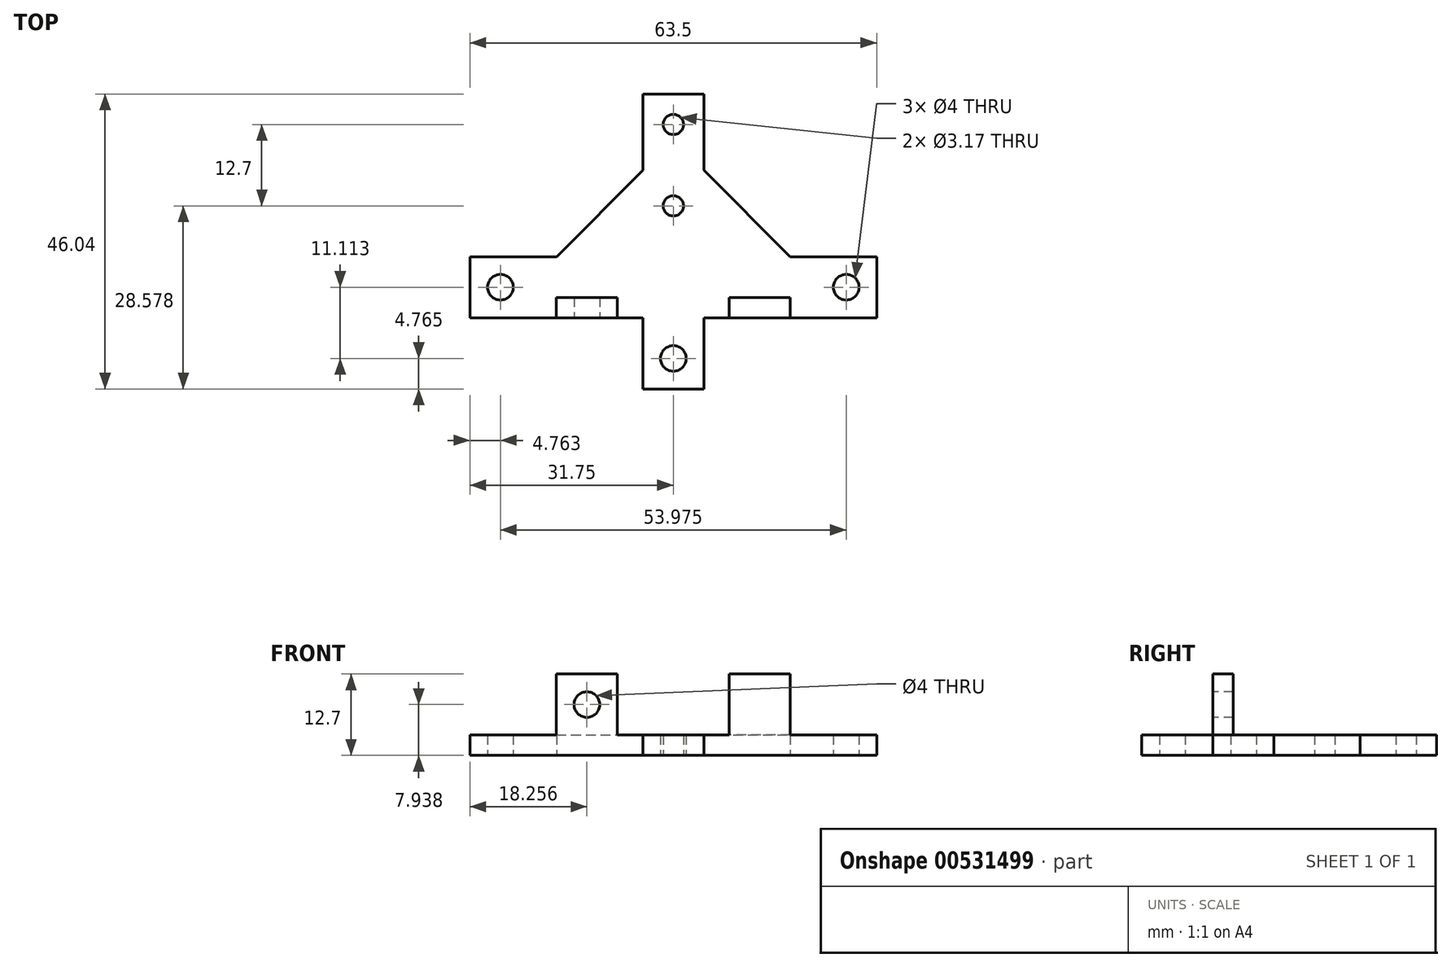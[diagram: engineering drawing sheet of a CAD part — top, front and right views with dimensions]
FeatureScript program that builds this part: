
annotation { "Feature Type Name" : "Feature", "Feature Type Description" : "" }
export const myFeature = defineFeature(function(context is Context, id is Id, definition is map)
    precondition{}
    {
        {
            var Q0;
            Q0=qCreatedBy(makeId("Top.planeOp"),FACE);
            var sketch = newSketch(context, id + "F0", { "sketchPlane" : qUnion([Q0])});
            skLineSegment(sketch, "E0.bottom", {"start": v(0, 0) * mm, "end": v(13.52, 0) * mm});
            skLineSegment(sketch, "E0.top", {"start": v(0, -9.53) * mm, "end": v(26.99, -9.53) * mm});
            skLineSegment(sketch, "E0.left", {"start": v(0, 0) * mm, "end": v(0, -9.53) * mm});
            skLineSegment(sketch, "E0.right", {"start": v(63.5, 0) * mm, "end": v(63.5, -9.52) * mm});
            skLineSegment(sketch, "E1.bottom", {"start": v(26.99, -20.64) * mm, "end": v(36.51, -20.64) * mm});
            skLineSegment(sketch, "E1.top", {"start": v(26.99, 25.4) * mm, "end": v(36.51, 25.4) * mm});
            skLineSegment(sketch, "E1.left", {"start": v(26.99, -20.64) * mm, "end": v(26.99, -9.52) * mm});
            skLineSegment(sketch, "E1.right", {"start": v(36.51, -20.64) * mm, "end": v(36.51, -9.52) * mm});
            skLineSegment(sketch, "E2.trimOffspring", {"start": v(26.99, 13.47) * mm, "end": v(26.99, 25.4) * mm});
            skLineSegment(sketch, "E3.trimOffspring", {"start": v(49.98, 0) * mm, "end": v(63.5, 0) * mm});
            skLineSegment(sketch, "E4.trimOffspring", {"start": v(36.51, 13.47) * mm, "end": v(36.51, 25.4) * mm});
            skLineSegment(sketch, "E5.trimOffspring", {"start": v(36.51, -9.53) * mm, "end": v(63.5, -9.53) * mm});
            skLineSegment(sketch, "E6", {"start": v(31.75, 25.4) * mm, "end": v(31.75, -20.64) * mm, "construction": true});
            skCircle(sketch, "E7", {"center": v(31.75, 20.64) * mm, "radius": 1.59 * mm});
            skCircle(sketch, "E8", {"center": v(31.75, 7.94) * mm, "radius": 1.59 * mm});
            skCircle(sketch, "E9", {"center": v(31.75, -15.87) * mm, "radius": 2 * mm});
            skCircle(sketch, "E10", {"center": v(4.76, -4.76) * mm, "radius": 2 * mm});
            skCircle(sketch, "E11", {"center": v(58.74, -4.76) * mm, "radius": 2 * mm});
            skLineSegment(sketch, "E12", {"start": v(4.76, -4.76) * mm, "end": v(58.74, -4.76) * mm, "construction": true});
            skLineSegment(sketch, "E13", {"start": v(13.52, 0) * mm, "end": v(26.99, 13.47) * mm});
            skLineSegment(sketch, "E14", {"start": v(36.51, 13.47) * mm, "end": v(49.98, 0) * mm});
            skLineSegment(sketch, "E15", {"start": v(0, 0) * mm, "end": v(9.53, -9.52) * mm, "construction": true});
            skLineSegment(sketch, "E16", {"start": v(63.5, 0) * mm, "end": v(53.98, -9.52) * mm, "construction": true});
            skSolve(sketch);
        }
        {
            var Q0;
            Q0 = qSketchRegion(id + "F0", true);
            extrude(context, id + "F1", {"entities" : qUnion([Q0]), "depth" : 3.17 * mm, "offsetDistance" : 25.4 * mm});
        }
        {
            var Q0;
            Q0=makeQuery(id+"F1.opExtrude","CAP_FACE",FACE,{"disambiguationData":[OSD([sQuery(id+"F0.wireOp",EDGE,"E0.bottom"),sQuery(id+"F0.wireOp",EDGE,"E0.top"),sQuery(id+"F0.wireOp",EDGE,"E0.left"),sQuery(id+"F0.wireOp",EDGE,"E0.right"),sQuery(id+"F0.wireOp",EDGE,"E1.bottom"),sQuery(id+"F0.wireOp",EDGE,"E1.top"),sQuery(id+"F0.wireOp",EDGE,"E1.left"),sQuery(id+"F0.wireOp",EDGE,"E1.right"),sQuery(id+"F0.wireOp",EDGE,"E2.trimOffspring"),sQuery(id+"F0.wireOp",EDGE,"E3.trimOffspring"),sQuery(id+"F0.wireOp",EDGE,"E4.trimOffspring"),sQuery(id+"F0.wireOp",EDGE,"E5.trimOffspring"),sQuery(id+"F0.wireOp",EDGE,"E7"),sQuery(id+"F0.wireOp",EDGE,"E8"),sQuery(id+"F0.wireOp",EDGE,"E9"),sQuery(id+"F0.wireOp",EDGE,"E10"),sQuery(id+"F0.wireOp",EDGE,"E11")])],"isStart":false});
            var sketch = newSketch(context, id + "F2", { "sketchPlane" : qUnion([Q0])});
            skLineSegment(sketch, "E17", {"start": v(31.75, -20.64) * mm, "end": v(31.75, 25.4) * mm, "construction": true});
            skLineSegment(sketch, "E18.bottom", {"start": v(13.5, -9.53) * mm, "end": v(23.02, -9.53) * mm});
            skLineSegment(sketch, "E18.top", {"start": v(13.5, -6.35) * mm, "end": v(23.02, -6.35) * mm});
            skLineSegment(sketch, "E18.left", {"start": v(13.5, -9.52) * mm, "end": v(13.5, -6.35) * mm});
            skLineSegment(sketch, "E18.right", {"start": v(23.02, -9.53) * mm, "end": v(23.02, -6.35) * mm});
            skLineSegment(sketch, "E19.MirrorCS", {"start": v(40.48, -9.53) * mm, "end": v(40.48, -6.35) * mm});
            skLineSegment(sketch, "E20.MirrorCS", {"start": v(50, -9.53) * mm, "end": v(40.48, -9.53) * mm});
            skLineSegment(sketch, "E21.MirrorCS", {"start": v(50, -6.35) * mm, "end": v(40.48, -6.35) * mm});
            skLineSegment(sketch, "E22.MirrorCS", {"start": v(50, -9.52) * mm, "end": v(50, -6.35) * mm});
            skSolve(sketch);
        }
        {
            var Q0;
            Q0 = qSketchRegion(id + "F2", true);
            extrude(context, id + "F3", {"entities" : qUnion([Q0]), "operationType" : NewBodyOperationType.ADD, "depth" : 9.52 * mm, "offsetDistance" : 25.4 * mm});
        }
        {
            var Q0;
            Q0=makeQuery(id+"F3.boolean.opBoolean","MERGE",FACE,{"derivedFrom":[makeQuery(id+"F1.opExtrude","SWEPT_FACE",FACE,{"disambiguationData":[OSD([sQuery(id+"F0.wireOp",EDGE,"E0.top")])]}),makeQuery(id+"F3.opExtrude","SWEPT_FACE",FACE,{"disambiguationData":[OSD([sQuery(id+"F2.wireOp",EDGE,"E18.bottom")])]})]});
            var sketch = newSketch(context, id + "F4", { "sketchPlane" : qUnion([Q0])});
            skLineSegment(sketch, "E23", {"start": v(18.26, 12.7) * mm, "end": v(18.26, 0) * mm, "construction": true});
            skCircle(sketch, "E24", {"center": v(18.26, 7.94) * mm, "radius": 2 * mm});
            skSolve(sketch);
        }
        {
            var Q0;
            Q0 = qSketchRegion(id + "F4", true);
            extrude(context, id + "F5", {"entities" : qUnion([Q0]), "operationType" : NewBodyOperationType.REMOVE, "endBound" : BoundingType.THROUGH_ALL, "oppositeDirection" : true, "depth" : 25.4 * mm, "offsetDistance" : 25.4 * mm});
        }
        {
            var Q0;
            Q0=makeQuery(id+"F1.opExtrude","SWEPT_FACE",FACE,{"disambiguationData":[OSD([sQuery(id+"F0.wireOp",EDGE,"E1.left")])]});
            cPlane(context, id + "F6", {"entities" : qUnion([Q0]), "cplaneType" : CPlaneType.OFFSET, "offset" : 3 / 406.4 * mm, "oppositeDirection" : true, "width" : 152.4 * mm, "height" : 152.4 * mm});
        }
    });
